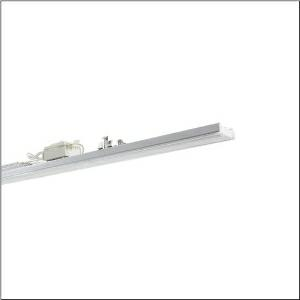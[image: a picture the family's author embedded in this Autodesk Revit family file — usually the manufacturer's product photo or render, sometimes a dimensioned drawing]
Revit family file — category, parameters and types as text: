
# Revit family: licross_r__11_recessed_ho_51te18mn4d5m_4063
name_source: partatom
category: Lighting Fixtures
units: mm (PartAtom-declared; Revit-internal decimal feet)

## family parameters
Cut with Voids When Loaded = No
Host = Face
Light Source = No
Part Type = Normal
Room Calculation Point = No
Round Connector Dimension = Use Diameter
Shared = No

## types (1)
- --- (1 x LED, 13950 lm, 74.5 W, 4000K)
    Apparent Load = 75 VA
    CIE Flux Codes = 78 94 99 100 100
    Color Rendering = 80
    Color Temperature = 4000K
    Default Elevation = 1800 mm
    Description = Licross® 11 Recessed HO, luminaire insert, of sheet steel, galvanised, coil coated, white, length: 1.500mm, width: 66mm, height: 67mm, LED rated luminous flux: 13.950lm, light colour: 840, control gear: ON/OFF Multilumen, with plug, 3-pole, with phase selection, mains connection: 220..240V, AC, 50/60Hz, rated input power: 75W, halogen-free wiring, primary light control with lens, of plastic, primary optical cover: cover, of PMMA, light emission: direct distribution, primary light characteristic: symmetric, protection rating (complete): IP54, insulation class (complete): insulation class I (protective earthing), certification: CE, ENEC, VDE, UKCA, protection symbol: D if used in an environment with non-conductive dust loads with corresponding accessories, impact resistance: IK06, permissible ambient temperature for indoor applications: -35..+35°C, corresponds to IFS (International Featured Standards) requirements for safety and quality in the food industry, reducing of maximum allowable ambient temperature of 5°C with ceiling mounting, packaging unit: 1 piece
    Height = 58 mm
    Lamp = 1 x LED
    Lamp Light Flux = 13950 lm
    Lamp Power = 74.5 W
    Lamp count = 1
    Length = 1500 mm
    Luminous efficacy = 187 lm/W
    Manufacturer = Siteco
    ModVariant = No
    Model = 51TE18MN4D5M
    Mounting Place = Ceiling
    Mounting Type = Pendant
    Number of Poles = 1
    OnlyDefault = Yes
    Power Factor = 1
    Product Name = Licross® 11 Recessed HO
    Product group = luminaire insert
    ProductGroupID = 902
    Protection Class = Protection class I
    Protection Degree = IP 54
    RLX_Detail_Level = 1
    RLX_Emergency_Light_Flux = 0 lm
    RLX_Emergency_Type = 0
    RLX_Emergency_Type_DB = No
    RlxData = <blob elided: 22209 chars, md5=42543228>
    Socket = socket
    Standby Power = 0 W
    System Light Flux = 13950 lm
    System Power = 75 W
    Type Comments = factory setting: luminous flux: 100 % | (A | C | E) | 174 mA
    Type Image = l_1296930.jpg
    URL = http://relux.com
    VarID = @adj_084714
    Voltage = 0 V
    Weight = 0.00 kg
    Width = 66 mm

## geometry (parser evidence)
native form markers: Blend x4, Sweep x9
no freeform markers — native parametric forms only
